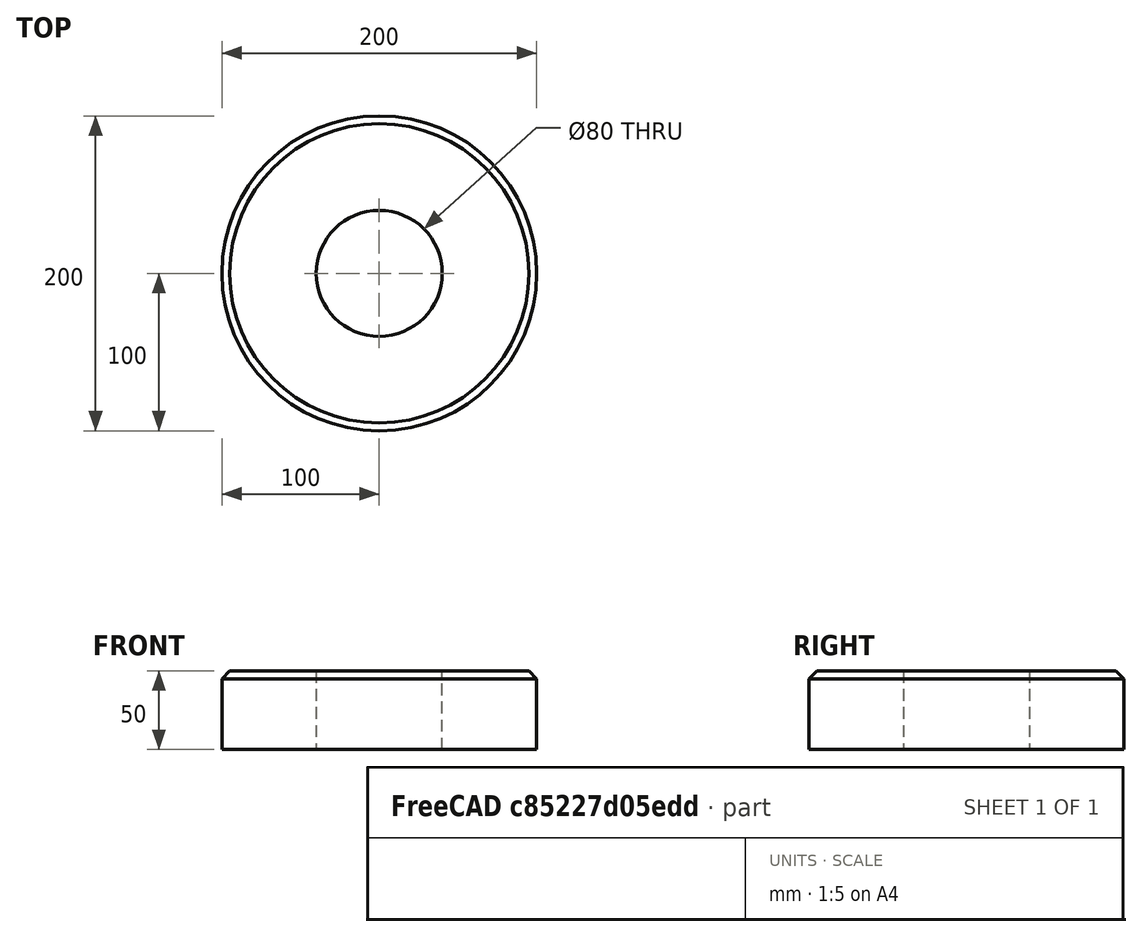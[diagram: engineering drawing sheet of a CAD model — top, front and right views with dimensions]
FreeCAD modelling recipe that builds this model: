
FCSTD DOCUMENT  (FreeCAD 0.18.4R)
Label: assembly_1
License: All rights reserved
LicenseURL: http://en.wikipedia.org/wiki/All_rights_reserved
objects: Sketcher::SketchObject×1, PartDesign::Pad×1, PartDesign::Chamfer×1, PartDesign::Body×1
note: 5 computed .brp shape members not serialized (recipe doc carries the construction recipe); baked Part::Feature solids carry a one-line shape summary decoded from their .brp

FEATURE [Sketcher::SketchObject] Sketch
  MapMode = 5
  Support = -> [XY_Plane]
  sketch-geometry (2):
    g0: Circle CenterX=0 CenterY=0 CenterZ=0 NormalX=0 NormalY=0 NormalZ=1 AngleXU=0 Radius=100
    g1: Circle CenterX=0 CenterY=0 CenterZ=0 NormalX=0 NormalY=0 NormalZ=1 AngleXU=0 Radius=40
  constraints (4):
    c: Coincident(g0,g-1)
    c: Radius(g0) = 100
    c: Coincident(g1,g0)
    c: Radius(g1) = 40
FEATURE [PartDesign::Pad] Pad
  Length = 50
  Length2 = 100
  Profile = -> Sketch
  Type = 0
FEATURE [PartDesign::Chamfer] Chamfer
  Base = -> Pad [Edge3]
  BaseFeature = -> Pad
  Size = 5
FEATURE [PartDesign::Body] Body
  Group = -> [Sketch,Pad,Chamfer]
  Origin = -> Origin
  Tip = -> Chamfer
